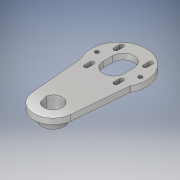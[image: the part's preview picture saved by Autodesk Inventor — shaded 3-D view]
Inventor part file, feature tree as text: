
AUTODESK INVENTOR PART (.ipt)
format: ipt  version: 2019.2 (Build 232265000, 265)  size: 247,808 bytes
history: native  units: mm
features: extrude x6, sketch x3, fillet x2, thread x2, plane x1
ambient origin geometry x8: Origin, YZ Plane, XZ Plane, XY Plane, X Axis, Y Axis, Z Axis, Center Point
bodies: Solid1 (feature_tree)
feature tree (14):
  sketch  "Sketch1"  dims[d1=57.0mm d2=20.0mm]
  plane  "Work Plane1"
  sketch  "Sketch2"  dims[d3=19.0mm d4=116.5mm]
  extrude  "Extrusion10"  Depth=20.0mm
  extrude  "Extrusion1"  Depth=116.5mm
  extrude  "Extrusion2"  Depth=2.0mm
  fillet  "Fillet1"  Radius=43.117mm
  thread  "Thread1"  [1 undecoded]
  thread  "Thread2"  [1 undecoded]
  extrude  "Extrusion6"  Depth=4.0mm
  fillet  "Fillet4"  Radius=3.0mm
  extrude  "Extrusion7"  Depth=4.0mm TaperAngle=0.0deg
  extrude  "Extrusion9"  Depth=2.0mm TaperAngle=0.0deg
  sketch  "Sketch6"  dims[d5=68.0mm d6=52.0mm d8=43.117mm d9=45.0mm d10=4.0mm d16=4.0mm d17=3.0mm d18=4.0mm d19=0.0mm d24=5.0mm d25=0.0mm d29=3.0mm d72=10.0mm d73=0.0mm d74=10.0mm d75=0.0mm d76=2.0mm d77=10.0mm d78=0.0mm d79=2.0mm d80=3.0mm d81=4.2mm d82=3.0mm d83=90.0deg d84=4.2mm d85=3.0mm d86=90.0deg d87=4.2mm d88=3.0mm d89=90.0deg d90=4.2mm d91=10.0mm d92=0.0mm d94=22.0mm d100=2.443461mm d101=1.2mm d102=10.0mm d103=0.0mm d104=2.0mm d105=0.0mm]
note: 2 required parameter values undecoded (feature->parameter linkage not recoverable at this tier; creation-order binding heuristic only, values carry confidence <= 0.55)
